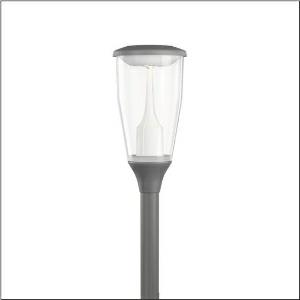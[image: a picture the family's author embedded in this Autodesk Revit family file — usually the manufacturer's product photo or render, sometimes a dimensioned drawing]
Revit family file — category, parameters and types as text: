
# Revit family: dl_11_iq___st1_2a_5xa5575kf14hp00022_6351
name_source: partatom
category: Lighting Fixtures
units: mm (PartAtom-declared; Revit-internal decimal feet)

## family parameters
Cut with Voids When Loaded = No
Host = Face
Light Source = No
Part Type = Normal
Room Calculation Point = No
Round Connector Dimension = Use Diameter
Shared = No

## types (1)
- --- (1 x LED, 5060 lm, 33.6 W, 4000K)
    Apparent Load = 34 VA
    CIE Flux Codes = 23 60 93 95 100
    Color Rendering = 70
    Color Temperature = 4000K
    Default Elevation = 1800 mm
    Description = DL 11 iQ, mast luminaire, Module 540 iQ-SR, primary light control with 3 zone facetted reflector, of plastic, silver coated, highly specular, structured, primary optical cover: cover, of PMMA, transparent, light distribution: ST1.2a, light emission: direct distribution, primary light characteristic: asymmetric, installation type: post-top, LED, High Power LED, light colour: 740, colour temperature: 4000K, control gear: iQ Street-Remote, control: Street-Remote, Auto-Match, Temp-Guard, Lumen-Switch, Night-Set, Smart-Wire, Light-Fading, Desk-Remote (wireless, voltage-free reading and setting of iQ features in the workshop via application-optimized NFC function/RFID function), optimised constant luminous flux control (CLO 2.0), mains connection: 220..240V, AC, 50/60Hz, connection cable pre-assembled, cable length: 5,5m, wiring characteristics: H07RN-F, 5-core, 1.5mm², start of lifetime: 34W, end of service life: 36W, luminaire housing, upper part, of diecast aluminium, coated, Siteco® metallic grey (DB 702S), spigot size: 76mm (post-top), mounting height: 3..5m, post-top mast mounting element, of diecast aluminium, coated, Siteco® metallic grey (DB 702S), Module 540 iQ-SR, traffic white (RAL 9016), equipment: Power, protection rating (complete): IP66, insulation class (complete): insulation class II (safety insulation), certification: CE, ENEC, ENEC+, VDE, impact resistance: IK07, packaging unit: 1 piece

Light Distribution: ST1.2a
    Height = 665 mm
    Lamp = 1 x LED
    Lamp Light Flux = 5060 lm
    Lamp Power = 33.6 W
    Lamp count = 1
    Length = 334 mm
    Luminous efficacy = 151 lm/W
    Manufacturer = Siteco
    ModVariant = No
    Model = 5XA5575KF14HP00022
    Number of Poles = 1
    OnlyDefault = Yes
    Power Factor = 1
    Product Name = DL 11 iQ | ST1.2a
    Product group = mast luminaire | pylon top
    ProductGroupID = 6100
    Protection Class = Protection class II
    Protection Degree = IP 66
    RLX_Detail_Level = 1
    RLX_Emergency_Light_Flux = 0 lm
    RLX_Emergency_Type = 0
    RLX_Emergency_Type_DB = No
    RlxData = <blob elided: 159925 chars, md5=204f7346>
    Socket = socket
    Standby Power = 0 W
    System Light Flux = 5060 lm
    System Power = 34 W
    Type Comments = factory setting: luminous flux: 100 % | dim-lin: 254 | 695 mA
    Type Image = l_1258354.jpg
    URL = http://relux.com
    VarID = @adj_033512
    Voltage = 0 V
    Weight = 0.00 kg
    Width = 0 mm  [stored 0 ft]

note: [stored X ft] marks values corroborated as IEEE doubles in the binary element streams (Revit-internal decimal feet)

## geometry (parser evidence)
native form markers: Blend x4, Sweep x8
no freeform markers — native parametric forms only
